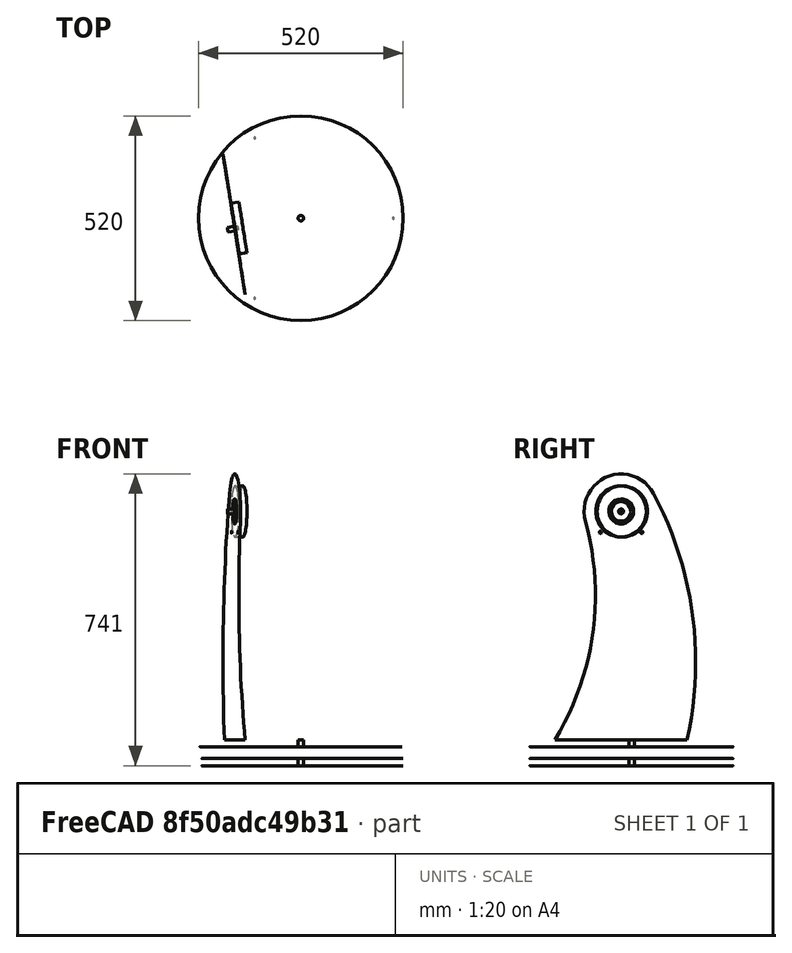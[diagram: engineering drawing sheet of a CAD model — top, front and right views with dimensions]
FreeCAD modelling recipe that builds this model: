
FCSTD DOCUMENT  (FreeCAD 2020.12.13R23076 +3015 (Git))
Label: teleskop
License: All rights reserved
LicenseURL: http://en.wikipedia.org/wiki/All_rights_reserved
objects: Part::FeaturePython×19, App::FeaturePython×13, App::Link×3
note: 18 computed .brp shape members not serialized (recipe doc carries the construction recipe); baked Part::Feature solids carry a one-line shape summary decoded from their .brp
EXTERNAL_REF file=zawieszenie-dol.fcstd obj=Assembly
EXTERNAL_REF file=zawieszenia-gora.fcstd obj=Assembly
EXTERNAL_REF file=tubus-kpl.FCStd obj=Assembly

FEATURE [App::Link] Link  label="zawieszenie-dol"
  LinkPlacement = pos=(-3.50003,-2.00002,205) rot=(0,0,1;0rad)
  LinkedObject = -> <external zawieszenie-dol.fcstd>#Assembly
  Placement = pos=(-3.50003,-2.00002,205) rot=(0,0,1;0rad)
  SyncGroupVisibility = false
  _LinkVersion = 1
FEATURE [App::Link] Link001  label="zawieszenie-gora"
  LinkPlacement = pos=(105.826,17.307,58.0003) rot=(0,0,1;0.156782rad)
  LinkedObject = -> <external zawieszenia-gora.fcstd>#Assembly
  Placement = pos=(105.826,17.307,58.0003) rot=(0,0,1;0.156782rad)
  SyncGroupVisibility = false
  _LinkVersion = 1
FEATURE [App::Link] Link002  label="tubus-kpl"
  LinkPlacement = pos=(89.4728,-455.647,570.496) rot=(-0.038514,0.490302,0.870701;3.27817rad)
  LinkedObject = -> <external tubus-kpl.FCStd>#Assembly
  Placement = pos=(89.4728,-455.647,570.496) rot=(-0.038514,0.490302,0.870701;3.27817rad)
  SyncGroupVisibility = false
  _LinkVersion = 1
FEATURE [Part::FeaturePython] Parts  # WARN: FeaturePython — macro-defined, semantics opaque (R4)
  Group = -> [Link,Link001,Link002]
  GroupMode = 0
  _LinkVersion = 1
FEATURE [Part::FeaturePython] Assembly  label="teleskop"  # WARN: FeaturePython — macro-defined, semantics opaque (R4)
  AutoRelax = true
  BuildShape = 0
  Freeze = false
  Group = -> [Constraints,Elements,Parts]
  Verbose = false
  _LinkVersion = 1
  _SolverType = 1
  _Version = 1
FEATURE [App::FeaturePython] Constraints  # WARN: FeaturePython — macro-defined, semantics opaque (R4)
  Group = -> [Constraint,Constraint001,Constraint002,Constraint003]
  _LinkVersion = 1
  _Version = 1
FEATURE [App::FeaturePython] Elements  # WARN: FeaturePython — macro-defined, semantics opaque (R4)
  Group = -> [_Element,_Element001,_Element002,_Element003,_Element004,_Element005,_Element006,_Element008,_Element010,_Element011,_Element012,_Element013,_Element016,_Element017,_Element018,_Element019,_Element020]
  _LinkVersion = 1
FEATURE [Part::FeaturePython] _Element  # link proxy (typed FeaturePython)
  Detach = false
  LinkTransform = true
  LinkedObject = -> Link001 [1.$Element025.]
  _LinkVersion = 1
  _Parent = -> Elements
FEATURE [Part::FeaturePython] _Element001  # link proxy (typed FeaturePython)
  Detach = false
  LinkTransform = true
  LinkedObject = -> Link [1.$Element.]
  _LinkVersion = 1
  _Parent = -> Elements
FEATURE [Part::FeaturePython] _Element002  # link proxy (typed FeaturePython)
  Detach = false
  LinkTransform = true
  LinkedObject = -> Link [1.$Element001.]
  _LinkVersion = 1
  _Parent = -> Elements
FEATURE [Part::FeaturePython] _Element003  # link proxy (typed FeaturePython)
  Detach = false
  LinkTransform = true
  LinkedObject = -> Link001 [1.$Element026.]
  _LinkVersion = 1
  _Parent = -> Elements
FEATURE [Part::FeaturePython] _Element004  # link proxy (typed FeaturePython)
  Detach = false
  LinkTransform = true
  LinkedObject = -> Link001 [1.$Element027.]
  _LinkVersion = 1
  _Parent = -> Elements
FEATURE [Part::FeaturePython] _Element005  # link proxy (typed FeaturePython)
  Detach = false
  LinkTransform = true
  LinkedObject = -> Link [1.$_Element017.]
  _LinkVersion = 1
  _Parent = -> Elements
FEATURE [Part::FeaturePython] _Element006  # link proxy (typed FeaturePython)
  Detach = false
  LinkTransform = true
  LinkedObject = -> Link002 [1.$Element.]
  _LinkVersion = 1
  _Parent = -> Elements
FEATURE [Part::FeaturePython] _Element008  # link proxy (typed FeaturePython)
  Detach = false
  LinkTransform = true
  LinkedObject = -> Link002 [1.$Element001.]
  _LinkVersion = 1
  _Parent = -> Elements
FEATURE [Part::FeaturePython] _Element010  # link proxy (typed FeaturePython)
  Detach = false
  LinkTransform = true
  LinkedObject = -> Link002 [1.$Element002.]
  _LinkVersion = 1
  _Parent = -> Elements
FEATURE [Part::FeaturePython] _Element011  # link proxy (typed FeaturePython)
  Detach = false
  LinkTransform = true
  LinkedObject = -> Link002 [1.$Element003.]
  _LinkVersion = 1
  _Parent = -> Elements
FEATURE [Part::FeaturePython] _Element012  # link proxy (typed FeaturePython)
  Detach = false
  LinkTransform = true
  LinkedObject = -> Link001 [1.$Element028.]
  _LinkVersion = 1
  _Parent = -> Elements
FEATURE [Part::FeaturePython] _Element013  # link proxy (typed FeaturePython)
  Detach = false
  LinkTransform = true
  LinkedObject = -> Link002 [1.$Element004.]
  _LinkVersion = 1
  _Parent = -> Elements
FEATURE [Part::FeaturePython] _Element016  # link proxy (typed FeaturePython)
  Detach = false
  LinkTransform = true
  LinkedObject = -> Link002 [1.$Element005.]
  _LinkVersion = 1
  _Parent = -> Elements
FEATURE [Part::FeaturePython] _Element017  # link proxy (typed FeaturePython)
  Detach = false
  LinkTransform = true
  LinkedObject = -> Link001 [1.$Element029.]
  _LinkVersion = 1
  _Parent = -> Elements
FEATURE [Part::FeaturePython] _Element018  # link proxy (typed FeaturePython)
  Detach = false
  LinkTransform = true
  LinkedObject = -> Link001 [1.$Element030.]
  _LinkVersion = 1
  _Parent = -> Elements
FEATURE [Part::FeaturePython] _Element019  # link proxy (typed FeaturePython)
  Detach = false
  LinkTransform = true
  LinkedObject = -> Link001 [1.$Element031.]
  _LinkVersion = 1
  _Parent = -> Elements
FEATURE [Part::FeaturePython] _Element020  # link proxy (typed FeaturePython)
  Detach = false
  LinkTransform = true
  LinkedObject = -> Link [1.$_Element018.]
  _LinkVersion = 1
  _Parent = -> Elements
FEATURE [App::FeaturePython] Constraint  label="Locked"  # WARN: FeaturePython — macro-defined, semantics opaque (R4)
  Disabled = false
  Group = -> [ElementLink]
  _ConstraintType = 0
  _LinkVersion = 1
  _Parent = -> Constraints
FEATURE [App::FeaturePython] ElementLink  label="_Element020"  # link proxy (typed FeaturePython)
  LinkTransform = true
  LinkedObject = -> _Element020
  _LinkVersion = 1
  _Parent = -> Constraint
FEATURE [App::FeaturePython] Constraint001  label="PlaneCoincident"  # WARN: FeaturePython — macro-defined, semantics opaque (R4)
  Angle = 0
  AnglePitch = 0
  AngleRoll = 0
  Cascade = false
  Disabled = false
  Group = -> [ElementLink001,ElementLink002]
  LockAngle = false
  Multiply = false
  Offset = -30
  OffsetX = 0
  OffsetY = 0
  _ConstraintType = 35
  _LinkVersion = 1
  _Parent = -> Constraints
FEATURE [App::FeaturePython] ElementLink001  label="_Element005"  # link proxy (typed FeaturePython)
  LinkTransform = true
  LinkedObject = -> _Element005
  _LinkVersion = 1
  _Parent = -> Constraint001
FEATURE [App::FeaturePython] ElementLink002  label="_Element004"  # link proxy (typed FeaturePython)
  LinkTransform = true
  LinkedObject = -> _Element004
  _LinkVersion = 1
  _Parent = -> Constraint001
FEATURE [App::FeaturePython] Constraint002  label="AxialAlignment"  # WARN: FeaturePython — macro-defined, semantics opaque (R4)
  Angle = 0
  AnglePitch = 0
  AngleRoll = 0
  Disabled = false
  Group = -> [ElementLink003,ElementLink004]
  LockAngle = false
  Multiply = false
  _ConstraintType = 36
  _LinkVersion = 1
  _Parent = -> Constraints
FEATURE [App::FeaturePython] ElementLink003  label="_Element006"  # link proxy (typed FeaturePython)
  LinkTransform = true
  LinkedObject = -> _Element006
  _LinkVersion = 1
  _Parent = -> Constraint002
FEATURE [App::FeaturePython] ElementLink004  label="_Element017"  # link proxy (typed FeaturePython)
  LinkTransform = true
  LinkedObject = -> _Element017
  _LinkVersion = 1
  _Parent = -> Constraint002
FEATURE [App::FeaturePython] Constraint003  label="PointInPlane"  # WARN: FeaturePython — macro-defined, semantics opaque (R4)
  Disabled = false
  Group = -> [ElementLink005,ElementLink006]
  _ConstraintType = 3
  _LinkVersion = 1
  _Parent = -> Constraints
FEATURE [App::FeaturePython] ElementLink005  label="_Element019"  # link proxy (typed FeaturePython)
  LinkTransform = true
  LinkedObject = -> _Element019
  _LinkVersion = 1
  _Parent = -> Constraint003
FEATURE [App::FeaturePython] ElementLink006  label="_Element010"  # link proxy (typed FeaturePython)
  LinkTransform = true
  LinkedObject = -> _Element010
  _LinkVersion = 1
  _Parent = -> Constraint003

RESOLVED EXTERNAL PARTS (link-assembly join: the EXTERNAL_REF files above that resolve inside this repo's crawl, each included once):
---- part tubus-kpl.FCStd = doc fcstd_3efcf8065df4 ----
FCSTD DOCUMENT  (FreeCAD 2020.12.13R23076 +3015 (Git))
Label: tubus-kpl
License: All rights reserved
LicenseURL: http://en.wikipedia.org/wiki/All_rights_reserved
objects: Part::FeaturePython×12, App::FeaturePython×8, App::Link×2
note: 11 computed .brp shape members not serialized (recipe doc carries the construction recipe); baked Part::Feature solids carry a one-line shape summary decoded from their .brp
EXTERNAL_REF file=tubus.fcstd obj=Body
EXTERNAL_REF file=wieniec-rury-mod1high.FCStd obj=Body

FEATURE [App::Link] Link  label="tubus"
  LinkPlacement = pos=(19.9999,-8.40128e-05,121) rot=(0,0.707107,0.707107;0rad)
  LinkedObject = -> <external tubus.fcstd>#Body
  Placement = pos=(19.9999,-8.40128e-05,121) rot=(0,0.707107,0.707107;0rad)
  SyncGroupVisibility = false
  _LinkVersion = 1
FEATURE [App::Link] Link001  label="wieniec-rury"
  LinkPlacement = pos=(155,-6.79195e-05,541) rot=(0.57735,0.57735,0.57735;2.0944rad)
  LinkedObject = -> <external wieniec-rury-mod1high.FCStd>#Body
  Placement = pos=(155,-6.79195e-05,541) rot=(0.57735,0.57735,0.57735;2.0944rad)
  SyncGroupVisibility = false
  _LinkVersion = 1
FEATURE [Part::FeaturePython] Parts  # WARN: FeaturePython — macro-defined, semantics opaque (R4)
  Group = -> [Link,Link001]
  GroupMode = 0
  _LinkVersion = 1
FEATURE [Part::FeaturePython] Assembly  label="tubus-kpl"  # WARN: FeaturePython — macro-defined, semantics opaque (R4)
  AutoRelax = true
  BuildShape = 0
  Freeze = true
  Group = -> [Constraints,Elements,Parts]
  Verbose = false
  _LinkVersion = 1
  _SolverType = 1
  _Version = 1
FEATURE [App::FeaturePython] Constraints  # WARN: FeaturePython — macro-defined, semantics opaque (R4)
  Group = -> [Constraint,Constraint001]
  _LinkVersion = 1
  _Version = 1
FEATURE [App::FeaturePython] Elements  # WARN: FeaturePython — macro-defined, semantics opaque (R4)
  Group = -> [_Element,_Element001,_Element002,_Element003,Element,Element001,Element002,Element003,Element004,Element005]
  _LinkVersion = 1
FEATURE [App::FeaturePython] Constraint  label="AxialAlignment"  # WARN: FeaturePython — macro-defined, semantics opaque (R4)
  Angle = 0
  AnglePitch = 0
  AngleRoll = 0
  Disabled = false
  Group = -> [ElementLink,ElementLink001]
  LockAngle = false
  Multiply = false
  _ConstraintType = 36
  _LinkVersion = 1
  _Parent = -> Constraints
FEATURE [App::FeaturePython] ElementLink  label="_Element"  # link proxy (typed FeaturePython)
  LinkTransform = true
  LinkedObject = -> _Element
  _LinkVersion = 1
  _Parent = -> Constraint
FEATURE [Part::FeaturePython] _Element  # link proxy (typed FeaturePython)
  Detach = false
  LinkTransform = true
  LinkedObject = -> Link001 [Pocket007.Face15]
  _LinkVersion = 1
  _Parent = -> Elements
FEATURE [App::FeaturePython] ElementLink001  label="_Element001"  # link proxy (typed FeaturePython)
  LinkTransform = true
  LinkedObject = -> _Element001
  _LinkVersion = 1
  _Parent = -> Constraint
FEATURE [Part::FeaturePython] _Element001  # link proxy (typed FeaturePython)
  Detach = false
  LinkTransform = true
  LinkedObject = -> Link [Pocket003.Face2]
  _LinkVersion = 1
  _Parent = -> Elements
FEATURE [App::FeaturePython] Constraint001  label="AxialAlignment001"  # WARN: FeaturePython — macro-defined, semantics opaque (R4)
  Angle = 0
  AnglePitch = 0
  AngleRoll = 0
  Disabled = false
  Group = -> [ElementLink002,ElementLink003]
  LockAngle = false
  Multiply = false
  _ConstraintType = 36
  _LinkVersion = 1
  _Parent = -> Constraints
FEATURE [App::FeaturePython] ElementLink002  label="_Element002"  # link proxy (typed FeaturePython)
  LinkTransform = true
  LinkedObject = -> _Element002
  _LinkVersion = 1
  _Parent = -> Constraint001
FEATURE [Part::FeaturePython] _Element002  # link proxy (typed FeaturePython)
  Detach = false
  LinkTransform = true
  LinkedObject = -> Link001 [Pocket007.Face6]
  _LinkVersion = 1
  _Parent = -> Elements
FEATURE [App::FeaturePython] ElementLink003  label="_Element003"  # link proxy (typed FeaturePython)
  LinkTransform = true
  LinkedObject = -> _Element003
  _LinkVersion = 1
  _Parent = -> Constraint001
FEATURE [Part::FeaturePython] _Element003  # link proxy (typed FeaturePython)
  Detach = false
  LinkTransform = true
  LinkedObject = -> Link [Pocket003.Face1]
  _LinkVersion = 1
  _Parent = -> Elements
FEATURE [Part::FeaturePython] Element  # link proxy (typed FeaturePython)
  Detach = false
  LinkTransform = true
  LinkedObject = -> Link [Pocket003.Face25]
  _LinkVersion = 1
  _Parent = -> Elements
FEATURE [Part::FeaturePython] Element001  # link proxy (typed FeaturePython)
  Detach = false
  LinkTransform = true
  LinkedObject = -> Link [Pocket003.Face14]
  _LinkVersion = 1
  _Parent = -> Elements
FEATURE [Part::FeaturePython] Element002  # link proxy (typed FeaturePython)
  Detach = false
  LinkTransform = true
  LinkedObject = -> Link [Pocket003.Face19]
  _LinkVersion = 1
  _Parent = -> Elements
FEATURE [Part::FeaturePython] Element003  # link proxy (typed FeaturePython)
  Detach = false
  LinkTransform = true
  LinkedObject = -> Link [Pocket003.Edge40]
  _LinkVersion = 1
  _Parent = -> Elements
FEATURE [Part::FeaturePython] Element004  # link proxy (typed FeaturePython)
  Detach = false
  LinkTransform = true
  LinkedObject = -> Link [Pocket003.Edge34]
  _LinkVersion = 1
  _Parent = -> Elements
FEATURE [Part::FeaturePython] Element005  # link proxy (typed FeaturePython)
  Detach = false
  LinkTransform = true
  LinkedObject = -> Link [Pocket003.Face10]
  _LinkVersion = 1
  _Parent = -> Elements
---- part zawieszenia-gora.fcstd = doc fcstd_c8abc18c9d7d (55000 chars; too large to inline — full recipe in that document) ----
---- part zawieszenie-dol.fcstd = doc fcstd_90b82e9d4289 ----
FCSTD DOCUMENT  (FreeCAD 2020.12.13R23076 +3015 (Git))
Label: zawieszenie-dol
License: All rights reserved
LicenseURL: http://en.wikipedia.org/wiki/All_rights_reserved
objects: App::FeaturePython×64, Part::FeaturePython×34, App::Link×12, App::LinkElement×6
note: 33 computed .brp shape members not serialized (recipe doc carries the construction recipe); baked Part::Feature solids carry a one-line shape summary decoded from their .brp
EXTERNAL_REF file=plyta-okr-dol.fcstd obj=Body
EXTERNAL_REF file=stopa.fcstd obj=Body
EXTERNAL_REF file=wieniec_mod1.FCStd obj=Body
EXTERNAL_REF file=tulejka-sruby.FCStd obj=Body
EXTERNAL_REF file=piasta-lozyska.FCStd obj=Body
EXTERNAL_REF file=lozysko 51126.FCStd obj=Assembly
EXTERNAL_REF file=regulacja-nogi.FCStd obj=Assembly

FEATURE [App::Link] Link  label="Link_plyta-okr-dol"
  LinkedObject = -> <external plyta-okr-dol.fcstd>#Body
  SyncGroupVisibility = false
  _LinkVersion = 1
FEATURE [App::Link] Link001  label="Link001_Assembly"
  LinkedObject = -> Assembly
  SyncGroupVisibility = false
  _LinkVersion = 1
FEATURE [App::Link] Link002  label="Link002_stopa"
  LinkPlacement = pos=(235,0,0) rot=(0,0,1;0rad)
  LinkedObject = -> <external stopa.fcstd>#Body
  Placement = pos=(235,0,0) rot=(0,0,1;0rad)
  SyncGroupVisibility = false
  _LinkVersion = 1
FEATURE [App::Link] Link003  label="Link003_Assembly"
  LinkedObject = -> Assembly
  SyncGroupVisibility = false
  _LinkVersion = 1
FEATURE [App::Link] Link004  label="Link004_Assembly"
  LinkedObject = -> Assembly
  SyncGroupVisibility = false
  _LinkVersion = 1
FEATURE [App::Link] Link005  label="Link005_stopa"
  LinkPlacement = pos=(-117.5,203.516,0) rot=(0,0,1;0rad)
  LinkedObject = -> <external stopa.fcstd>#Body
  Placement = pos=(-117.5,203.516,0) rot=(0,0,1;0rad)
  SyncGroupVisibility = false
  _LinkVersion = 1
FEATURE [App::Link] Link006  label="Link006_stopa"
  LinkPlacement = pos=(-117.5,-203.516,0) rot=(0,0,1;0rad)
  LinkedObject = -> <external stopa.fcstd>#Body
  Placement = pos=(-117.5,-203.516,0) rot=(0,0,1;0rad)
  SyncGroupVisibility = false
  _LinkVersion = 1
FEATURE [App::Link] Link008  label="tulejka-sruby"
  LinkPlacement = pos=(0,0,-4.40707e-10) rot=(0,0,1;0rad)
  LinkedObject = -> <external tulejka-sruby.FCStd>#Body
  Placement = pos=(0,0,-4.40707e-10) rot=(0,0,1;0rad)
  SyncGroupVisibility = false
  _LinkVersion = 1
FEATURE [App::Link] Link009  label="piasta-lozyska"
  LinkPlacement = pos=(0,0,18) rot=(0,0,1;0rad)
  LinkedObject = -> <external piasta-lozyska.FCStd>#Body
  Placement = pos=(0,0,18) rot=(0,0,1;0rad)
  SyncGroupVisibility = false
  _LinkVersion = 1
FEATURE [App::Link] Link010  label="51126-lozysko"
  LinkPlacement = pos=(0,0,18) rot=(0,-1,0;1.5708rad)
  LinkedObject = -> <external lozysko 51126.FCStd>#Assembly
  Placement = pos=(0,0,18) rot=(0,-1,0;1.5708rad)
  SyncGroupVisibility = false
  _LinkVersion = 1
FEATURE [App::LinkElement] Link011_i0
  LinkPlacement = pos=(0,0,1.8261e-12) rot=(0,0,1;0rad)
  LinkedObject = -> <external regulacja-nogi.FCStd>#Assembly
  Placement = pos=(0,0,1.8261e-12) rot=(0,0,1;0rad)
  _LinkVersion = 1
FEATURE [App::LinkElement] Link011_i1
  LinkPlacement = pos=(-203.516,-352.5,1.8296e-12) rot=(0,0,-1;1.0472rad)
  LinkedObject = -> <external regulacja-nogi.FCStd>#Assembly
  Placement = pos=(-203.516,-352.5,1.8296e-12) rot=(0,0,-1;1.0472rad)
  _LinkVersion = 1
FEATURE [App::LinkElement] Link011_i2
  LinkPlacement = pos=(203.516,-352.5,1.8296e-12) rot=(0,0,1;1.0472rad)
  LinkedObject = -> <external regulacja-nogi.FCStd>#Assembly
  Placement = pos=(203.516,-352.5,1.8296e-12) rot=(0,0,1;1.0472rad)
  _LinkVersion = 1
FEATURE [App::Link] Link011  label="regulacja-nogi"
  ElementCount = 3
  ElementList = -> [Link011_i0,Link011_i1,Link011_i2]
  LinkPlacement = pos=(235,0,-20) rot=(0.707107,0.707107,0;3.14159rad)
  LinkedObject = -> <external regulacja-nogi.FCStd>#Assembly
  Placement = pos=(235,0,-20) rot=(0.707107,0.707107,0;3.14159rad)
  SyncGroupVisibility = false
  _LinkVersion = 1
FEATURE [App::LinkElement] Link007_i0
  LinkPlacement = pos=(0,0,-3.6e-15) rot=(0,0,-1;5.65256rad)
  LinkedObject = -> <external wieniec_mod1.FCStd>#Body
  Placement = pos=(0,0,-3.6e-15) rot=(0,0,-1;5.65256rad)
  _LinkVersion = 0
FEATURE [App::LinkElement] Link007_i1
  LinkPlacement = pos=(2e-16,8e-16,3.6e-15) rot=(0,0,-1;4.77196rad)
  LinkedObject = -> <external wieniec_mod1.FCStd>#Body
  Placement = pos=(2e-16,8e-16,3.6e-15) rot=(0,0,-1;4.77196rad)
  _LinkVersion = 0
FEATURE [App::LinkElement] Link007_i2
  LinkPlacement = pos=(-1.93e-14,2.3e-15,2.49e-14) rot=(0,0,-1;0.249973rad)
  LinkedObject = -> <external wieniec_mod1.FCStd>#Body
  Placement = pos=(-1.93e-14,2.3e-15,2.49e-14) rot=(0,0,-1;0.249973rad)
  _LinkVersion = 0
FEATURE [App::Link] Link007  label="wieniec"
  ElementCount = 3
  ElementList = -> [Link007_i0,Link007_i1,Link007_i2]
  LinkPlacement = pos=(0,0,22) rot=(0.991445,-0.130526,0;3.14159rad)
  LinkedObject = -> <external wieniec_mod1.FCStd>#Body
  Placement = pos=(0,0,22) rot=(0.991445,-0.130526,0;3.14159rad)
  SyncGroupVisibility = false
  _LinkVersion = 1
FEATURE [Part::FeaturePython] Parts  # WARN: FeaturePython — macro-defined, semantics opaque (R4)
  Group = -> [Link,Link002,Link005,Link006,Link007,Link008,Link009,Link010,Link011]
  GroupMode = 0
  _LinkVersion = 1
FEATURE [Part::FeaturePython] Assembly  label="zawieszenie-dol"  # WARN: FeaturePython — macro-defined, semantics opaque (R4)
  AutoRelax = true
  BuildShape = 0
  Freeze = true
  Group = -> [Constraints,Elements,Parts]
  Verbose = false
  _LinkVersion = 1
  _SolverType = 1
FEATURE [App::FeaturePython] Constraints  # WARN: FeaturePython — macro-defined, semantics opaque (R4)
  Group = -> [Constraint001,Constraint002,Constraint003,Constraint004,Constraint005,Constraint006,Constraint,Constraint011,Constraint012,Constraint013,Constraint014,Constraint015,Constraint016,Constraint017,Constraint018,Constraint019,Constraint020,Constraint021,Constraint022,Constraint023,Constraint024]
  _LinkVersion = 1
  _Version = 1
FEATURE [App::FeaturePython] Elements  # WARN: FeaturePython — macro-defined, semantics opaque (R4)
  Group = -> [_Element,_Element001,_Element002,_Element003,_Element004,_Element005,_Element006,_Element007,_Element008,_Element009,_Element011,_Element013,_Element015,_Element017,Element,Element001,_Element018,_Element019,_Element020,_Element021,_Element022,_Element023,_Element024,_Element025,_Element026,_Element027,_Element028,_Element029,_Element030,_Element031,_Element032,_Element033]
  _LinkVersion = 1
FEATURE [Part::FeaturePython] _Element  # link proxy (typed FeaturePython)
  Detach = false
  LinkTransform = true
  LinkedObject = -> Link [PolarPattern.Face2]
  _LinkVersion = 1
  _Parent = -> Elements
FEATURE [App::FeaturePython] Constraint001  label="AxialAlignment"  # WARN: FeaturePython — macro-defined, semantics opaque (R4)
  Angle = 0
  AnglePitch = 0
  AngleRoll = 0
  Disabled = false
  Group = -> [ElementLink001,ElementLink002]
  LockAngle = false
  Multiply = false
  _ConstraintType = 36
  _LinkVersion = 1
  _Parent = -> Constraints
FEATURE [App::FeaturePython] ElementLink001  label="_Element001"  # link proxy (typed FeaturePython)
  LinkTransform = true
  LinkedObject = -> _Element001
  _LinkVersion = 1
  _Parent = -> Constraint001
FEATURE [Part::FeaturePython] _Element001  # link proxy (typed FeaturePython)
  Detach = false
  LinkTransform = true
  LinkedObject = -> Link005 [Revolution.Edge1]
  _LinkVersion = 1
  _Parent = -> Elements
FEATURE [App::FeaturePython] ElementLink002  label="_Element002"  # link proxy (typed FeaturePython)
  LinkTransform = true
  LinkedObject = -> _Element002
  _LinkVersion = 1
  _Parent = -> Constraint001
FEATURE [Part::FeaturePython] _Element002  # link proxy (typed FeaturePython)
  Detach = false
  LinkTransform = true
  LinkedObject = -> Link [PolarPattern.Edge6]
  _LinkVersion = 1
  _Parent = -> Elements
FEATURE [App::FeaturePython] Constraint002  label="PlaneAlignment"  # WARN: FeaturePython — macro-defined, semantics opaque (R4)
  Angle = 0
  AnglePitch = 0
  AngleRoll = 0
  Cascade = false
  Disabled = false
  Group = -> [ElementLink003,ElementLink004]
  LockAngle = false
  _ConstraintType = 37
  _LinkVersion = 1
  _Parent = -> Constraints
FEATURE [App::FeaturePython] ElementLink003  label="_Element"  # link proxy (typed FeaturePython)
  LinkTransform = true
  LinkedObject = -> _Element
  _LinkVersion = 1
  _Parent = -> Constraint002
FEATURE [App::FeaturePython] ElementLink004  label="_Element003"  # link proxy (typed FeaturePython)
  LinkTransform = true
  LinkedObject = -> _Element003
  _LinkVersion = 1
  _Parent = -> Constraint002
FEATURE [Part::FeaturePython] _Element003  # link proxy (typed FeaturePython)
  Detach = false
  LinkTransform = true
  LinkedObject = -> Link005 [Revolution.Face1]
  _LinkVersion = 1
  _Parent = -> Elements
FEATURE [App::FeaturePython] Constraint003  label="AxialAlignment001"  # WARN: FeaturePython — macro-defined, semantics opaque (R4)
  Angle = 0
  AnglePitch = 0
  AngleRoll = 0
  Disabled = false
  Group = -> [ElementLink005,ElementLink006]
  LockAngle = false
  Multiply = false
  _ConstraintType = 36
  _LinkVersion = 1
  _Parent = -> Constraints
FEATURE [App::FeaturePython] ElementLink005  label="_Element004"  # link proxy (typed FeaturePython)
  LinkTransform = true
  LinkedObject = -> _Element004
  _LinkVersion = 1
  _Parent = -> Constraint003
FEATURE [Part::FeaturePython] _Element004  # link proxy (typed FeaturePython)
  Detach = false
  LinkTransform = true
  LinkedObject = -> Link006 [Revolution.Edge1]
  _LinkVersion = 1
  _Parent = -> Elements
FEATURE [App::FeaturePython] ElementLink006  label="_Element005"  # link proxy (typed FeaturePython)
  LinkTransform = true
  LinkedObject = -> _Element005
  _LinkVersion = 1
  _Parent = -> Constraint003
FEATURE [Part::FeaturePython] _Element005  # link proxy (typed FeaturePython)
  Detach = false
  LinkTransform = true
  LinkedObject = -> Link [PolarPattern.Edge4]
  _LinkVersion = 1
  _Parent = -> Elements
FEATURE [App::FeaturePython] Constraint004  label="PlaneAlignment001"  # WARN: FeaturePython — macro-defined, semantics opaque (R4)
  Angle = 0
  AnglePitch = 0
  AngleRoll = 0
  Cascade = false
  Disabled = false
  Group = -> [ElementLink007,ElementLink008]
  LockAngle = false
  _ConstraintType = 37
  _LinkVersion = 1
  _Parent = -> Constraints
FEATURE [App::FeaturePython] ElementLink007  label="_Element"  # link proxy (typed FeaturePython)
  LinkTransform = true
  LinkedObject = -> _Element
  _LinkVersion = 1
  _Parent = -> Constraint004
FEATURE [App::FeaturePython] ElementLink008  label="_Element006"  # link proxy (typed FeaturePython)
  LinkTransform = true
  LinkedObject = -> _Element006
  _LinkVersion = 1
  _Parent = -> Constraint004
FEATURE [Part::FeaturePython] _Element006  # link proxy (typed FeaturePython)
  Detach = false
  LinkTransform = true
  LinkedObject = -> Link006 [Revolution.Face1]
  _LinkVersion = 1
  _Parent = -> Elements
FEATURE [App::FeaturePython] Constraint005  label="AxialAlignment002"  # WARN: FeaturePython — macro-defined, semantics opaque (R4)
  Angle = 0
  AnglePitch = 0
  AngleRoll = 0
  Disabled = false
  Group = -> [ElementLink009,ElementLink010]
  LockAngle = false
  Multiply = false
  _ConstraintType = 36
  _LinkVersion = 1
  _Parent = -> Constraints
FEATURE [App::FeaturePython] ElementLink009  label="_Element007"  # link proxy (typed FeaturePython)
  LinkTransform = true
  LinkedObject = -> _Element007
  _LinkVersion = 1
  _Parent = -> Constraint005
FEATURE [Part::FeaturePython] _Element007  # link proxy (typed FeaturePython)
  Detach = false
  LinkTransform = true
  LinkedObject = -> Link002 [Revolution.Edge1]
  _LinkVersion = 1
  _Parent = -> Elements
FEATURE [App::FeaturePython] ElementLink010  label="_Element008"  # link proxy (typed FeaturePython)
  LinkTransform = true
  LinkedObject = -> _Element008
  _LinkVersion = 1
  _Parent = -> Constraint005
FEATURE [Part::FeaturePython] _Element008  # link proxy (typed FeaturePython)
  Detach = false
  LinkTransform = true
  LinkedObject = -> Link [PolarPattern.Edge5]
  _LinkVersion = 1
  _Parent = -> Elements
FEATURE [App::FeaturePython] Constraint006  label="PlaneAlignment002"  # WARN: FeaturePython — macro-defined, semantics opaque (R4)
  Angle = 0
  AnglePitch = 0
  AngleRoll = 0
  Cascade = false
  Disabled = false
  Group = -> [ElementLink011,ElementLink012]
  LockAngle = false
  _ConstraintType = 37
  _LinkVersion = 1
  _Parent = -> Constraints
FEATURE [App::FeaturePython] ElementLink011  label="_Element"  # link proxy (typed FeaturePython)
  LinkTransform = true
  LinkedObject = -> _Element
  _LinkVersion = 1
  _Parent = -> Constraint006
FEATURE [App::FeaturePython] ElementLink012  label="_Element009"  # link proxy (typed FeaturePython)
  LinkTransform = true
  LinkedObject = -> _Element009
  _LinkVersion = 1
  _Parent = -> Constraint006
FEATURE [Part::FeaturePython] _Element009  # link proxy (typed FeaturePython)
  Detach = false
  LinkTransform = true
  LinkedObject = -> Link002 [Revolution.Face1]
  _LinkVersion = 1
  _Parent = -> Elements
FEATURE [Part::FeaturePython] _Element011  # link proxy (typed FeaturePython)
  Detach = false
  LinkTransform = true
  LinkedObject = -> Link [PolarPattern.Face1]
  _LinkVersion = 1
  _Parent = -> Elements
FEATURE [Part::FeaturePython] _Element013  # link proxy (typed FeaturePython)
  Detach = false
  LinkTransform = true
  LinkedObject = -> Link [PolarPattern.Face3]
  _LinkVersion = 1
  _Parent = -> Elements
FEATURE [Part::FeaturePython] _Element015  # link proxy (typed FeaturePython)
  Detach = false
  LinkTransform = true
  LinkedObject = -> Link [Pocket001.Face1]
  _LinkVersion = 1
  _Parent = -> Elements
FEATURE [Part::FeaturePython] _Element017  # link proxy (typed FeaturePython)
  Detach = false
  LinkTransform = true
  LinkedObject = -> Link [Pocket001.Face3]
  _LinkVersion = 1
  _Parent = -> Elements
FEATURE [Part::FeaturePython] Element  # link proxy (typed FeaturePython)
  Detach = false
  LinkTransform = true
  LinkedObject = -> Link [Pocket001.Face5]
  _LinkVersion = 1
  _Parent = -> Elements
FEATURE [Part::FeaturePython] Element001  # link proxy (typed FeaturePython)
  Detach = false
  LinkTransform = true
  LinkedObject = -> Link [Pocket001.Edge5]
  _LinkVersion = 1
  _Parent = -> Elements
FEATURE [App::FeaturePython] Constraint  label="Locked"  # WARN: FeaturePython — macro-defined, semantics opaque (R4)
  Disabled = false
  Group = -> [ElementLink]
  _ConstraintType = 0
  _LinkVersion = 1
  _Parent = -> Constraints
FEATURE [App::FeaturePython] ElementLink  label="_Element018"  # link proxy (typed FeaturePython)
  LinkTransform = true
  LinkedObject = -> _Element018
  _LinkVersion = 1
  _Parent = -> Constraint
FEATURE [Part::FeaturePython] _Element018  # link proxy (typed FeaturePython)
  Detach = false
  LinkTransform = true
  LinkedObject = -> Link [Pocket001.Face2]
  _LinkVersion = 1
  _Parent = -> Elements
FEATURE [Part::FeaturePython] _Element019  # link proxy (typed FeaturePython)
  Detach = false
  LinkTransform = true
  LinkedObject = -> Link008 [Chamfer.Face1]
  _LinkVersion = 1
  _Parent = -> Elements
FEATURE [Part::FeaturePython] _Element020  # link proxy (typed FeaturePython)
  Detach = false
  LinkTransform = true
  LinkedObject = -> Link008 [Chamfer.Face3]
  _LinkVersion = 1
  _Parent = -> Elements
FEATURE [App::FeaturePython] Constraint011  label="PlaneCoincident"  # WARN: FeaturePython — macro-defined, semantics opaque (R4)
  Angle = 0
  AnglePitch = 0
  AngleRoll = 0
  Cascade = false
  Disabled = false
  Group = -> [ElementLink021,ElementLink022]
  LockAngle = false
  Multiply = false
  OffsetX = 0
  OffsetY = 0
  _ConstraintType = 35
  _LinkVersion = 1
  _Parent = -> Constraints
FEATURE [App::FeaturePython] ElementLink021  label="_Element021"  # link proxy (typed FeaturePython)
  LinkTransform = true
  LinkedObject = -> _Element021
  _LinkVersion = 1
  _Parent = -> Constraint011
FEATURE [Part::FeaturePython] _Element021  # link proxy (typed FeaturePython)
  Detach = false
  LinkTransform = true
  LinkedObject = -> Link009 [Pocket002.Face1]
  _LinkVersion = 1
  _Parent = -> Elements
FEATURE [App::FeaturePython] ElementLink022  label="_Element017"  # link proxy (typed FeaturePython)
  LinkTransform = true
  LinkedObject = -> _Element017
  _LinkVersion = 1
  _Parent = -> Constraint011
FEATURE [App::FeaturePython] Constraint012  label="PlaneCoincident001"  # WARN: FeaturePython — macro-defined, semantics opaque (R4)
  Angle = 0
  AnglePitch = 0
  AngleRoll = 0
  Cascade = false
  Disabled = false
  Group = -> [ElementLink023,ElementLink024]
  LockAngle = false
  Multiply = false
  OffsetX = 0
  OffsetY = 0
  _ConstraintType = 35
  _LinkVersion = 1
  _Parent = -> Constraints
FEATURE [App::FeaturePython] ElementLink023  label="_Element020"  # link proxy (typed FeaturePython)
  LinkTransform = true
  LinkedObject = -> _Element020
  _LinkVersion = 1
  _Parent = -> Constraint012
FEATURE [App::FeaturePython] ElementLink024  label="_Element018"  # link proxy (typed FeaturePython)
  LinkTransform = true
  LinkedObject = -> _Element018
  _LinkVersion = 1
  _Parent = -> Constraint012
FEATURE [App::FeaturePython] Constraint013  label="PlaneCoincident002"  # WARN: FeaturePython — macro-defined, semantics opaque (R4)
  Angle = 0
  AnglePitch = 0
  AngleRoll = 0
  Cascade = false
  Disabled = false
  Group = -> [ElementLink025,ElementLink026]
  LockAngle = false
  Multiply = false
  OffsetX = 0
  OffsetY = 0
  _ConstraintType = 35
  _LinkVersion = 1
  _Parent = -> Constraints
FEATURE [App::FeaturePython] ElementLink025  label="_Element022"  # link proxy (typed FeaturePython)
  LinkTransform = true
  LinkedObject = -> _Element022
  _LinkVersion = 1
  _Parent = -> Constraint013
FEATURE [Part::FeaturePython] _Element022  # link proxy (typed FeaturePython)
  Detach = false
  LinkTransform = true
  LinkedObject = -> Link010 [1.$Element.]
  _LinkVersion = 1
  _Parent = -> Elements
FEATURE [App::FeaturePython] ElementLink026  label="_Element017"  # link proxy (typed FeaturePython)
  LinkTransform = true
  LinkedObject = -> _Element017
  _LinkVersion = 1
  _Parent = -> Constraint013
FEATURE [Part::FeaturePython] _Element023  # link proxy (typed FeaturePython)
  Detach = false
  LinkTransform = true
  LinkedObject = -> Link [Pocket001.Edge6]
  _LinkVersion = 1
  _Parent = -> Elements
FEATURE [App::FeaturePython] Constraint014  label="PlaneCoincident003"  # WARN: FeaturePython — macro-defined, semantics opaque (R4)
  Angle = 0
  AnglePitch = 0
  AngleRoll = 0
  Cascade = false
  Disabled = false
  Group = -> [ElementLink027,ElementLink028]
  LockAngle = false
  Multiply = false
  OffsetX = 0
  OffsetY = 0
  _ConstraintType = 35
  _LinkVersion = 1
  _Parent = -> Constraints
FEATURE [App::FeaturePython] ElementLink027  label="_Element024"  # link proxy (typed FeaturePython)
  LinkTransform = true
  LinkedObject = -> _Element024
  _LinkVersion = 1
  _Parent = -> Constraint014
FEATURE [Part::FeaturePython] _Element024  # link proxy (typed FeaturePython)
  Detach = false
  LinkTransform = true
  LinkedObject = -> Link011 [0.1.$Element002.]
  _LinkVersion = 1
  _Parent = -> Elements
FEATURE [App::FeaturePython] ElementLink028  label="_Element009"  # link proxy (typed FeaturePython)
  LinkTransform = true
  LinkedObject = -> _Element009
  _LinkVersion = 1
  _Parent = -> Constraint014
FEATURE [App::FeaturePython] Constraint015  label="PlaneCoincident004"  # WARN: FeaturePython — macro-defined, semantics opaque (R4)
  Angle = 0
  AnglePitch = 0
  AngleRoll = 0
  Cascade = false
  Disabled = false
  Group = -> [ElementLink029,ElementLink030]
  LockAngle = false
  Multiply = false
  OffsetX = 0
  OffsetY = 0
  _ConstraintType = 35
  _LinkVersion = 1
  _Parent = -> Constraints
FEATURE [App::FeaturePython] ElementLink029  label="_Element025"  # link proxy (typed FeaturePython)
  LinkTransform = true
  LinkedObject = -> _Element025
  _LinkVersion = 1
  _Parent = -> Constraint015
FEATURE [Part::FeaturePython] _Element025  # link proxy (typed FeaturePython)
  Detach = false
  LinkTransform = true
  LinkedObject = -> Link011 [2.1.$Element002.]
  _LinkVersion = 1
  _Parent = -> Elements
FEATURE [App::FeaturePython] ElementLink030  label="_Element003"  # link proxy (typed FeaturePython)
  LinkTransform = true
  LinkedObject = -> _Element003
  _LinkVersion = 1
  _Parent = -> Constraint015
FEATURE [App::FeaturePython] Constraint016  label="PlaneCoincident005"  # WARN: FeaturePython — macro-defined, semantics opaque (R4)
  Angle = 0
  AnglePitch = 0
  AngleRoll = 0
  Cascade = false
  Disabled = false
  Group = -> [ElementLink031,ElementLink032]
  LockAngle = false
  Multiply = false
  OffsetX = 0
  OffsetY = 0
  _ConstraintType = 35
  _LinkVersion = 1
  _Parent = -> Constraints
FEATURE [App::FeaturePython] ElementLink031  label="_Element006"  # link proxy (typed FeaturePython)
  LinkTransform = true
  LinkedObject = -> _Element006
  _LinkVersion = 1
  _Parent = -> Constraint016
FEATURE [App::FeaturePython] ElementLink032  label="_Element026"  # link proxy (typed FeaturePython)
  LinkTransform = true
  LinkedObject = -> _Element026
  _LinkVersion = 1
  _Parent = -> Constraint016
FEATURE [Part::FeaturePython] _Element026  # link proxy (typed FeaturePython)
  Detach = false
  LinkTransform = true
  LinkedObject = -> Link011 [1.1.$Element002.]
  _LinkVersion = 1
  _Parent = -> Elements
FEATURE [App::FeaturePython] Constraint017  label="AxialAlignment003"  # WARN: FeaturePython — macro-defined, semantics opaque (R4)
  Angle = 0
  AnglePitch = 0
  AngleRoll = 0
  Disabled = false
  Group = -> [ElementLink033,ElementLink034]
  LockAngle = false
  Multiply = false
  _ConstraintType = 36
  _LinkVersion = 0
  _Parent = -> Constraints
FEATURE [App::FeaturePython] ElementLink033  label="_Element027"  # link proxy (typed FeaturePython)
  LinkTransform = true
  LinkedObject = -> _Element027
  _LinkVersion = 0
  _Parent = -> Constraint017
FEATURE [Part::FeaturePython] _Element027  # link proxy (typed FeaturePython)
  Detach = false
  LinkTransform = true
  LinkedObject = -> Link007 [2.Pocket003.Face3]
  _LinkVersion = 0
  _Parent = -> Elements
FEATURE [App::FeaturePython] ElementLink034  label="_Element015"  # link proxy (typed FeaturePython)
  LinkTransform = true
  LinkedObject = -> _Element015
  _LinkVersion = 0
  _Parent = -> Constraint017
FEATURE [App::FeaturePython] Constraint018  label="AxialAlignment004"  # WARN: FeaturePython — macro-defined, semantics opaque (R4)
  Angle = 0
  AnglePitch = 0
  AngleRoll = 0
  Disabled = false
  Group = -> [ElementLink035,ElementLink036]
  LockAngle = false
  Multiply = false
  _ConstraintType = 36
  _LinkVersion = 0
  _Parent = -> Constraints
FEATURE [App::FeaturePython] ElementLink035  label="_Element028"  # link proxy (typed FeaturePython)
  LinkTransform = true
  LinkedObject = -> _Element028
  _LinkVersion = 0
  _Parent = -> Constraint018
FEATURE [Part::FeaturePython] _Element028  # link proxy (typed FeaturePython)
  Detach = false
  LinkTransform = true
  LinkedObject = -> Link007 [0.Pocket003.Face3]
  _LinkVersion = 0
  _Parent = -> Elements
FEATURE [App::FeaturePython] ElementLink036  label="_Element015"  # link proxy (typed FeaturePython)
  LinkTransform = true
  LinkedObject = -> _Element015
  _LinkVersion = 0
  _Parent = -> Constraint018
FEATURE [App::FeaturePython] Constraint019  label="PointInPlane"  # WARN: FeaturePython — macro-defined, semantics opaque (R4)
  Disabled = false
  Group = -> [ElementLink037,ElementLink038]
  _ConstraintType = 3
  _LinkVersion = 0
  _Parent = -> Constraints
FEATURE [App::FeaturePython] ElementLink037  label="_Element029"  # link proxy (typed FeaturePython)
  LinkTransform = true
  LinkedObject = -> _Element029
  _LinkVersion = 0
  _Parent = -> Constraint019
FEATURE [Part::FeaturePython] _Element029  # link proxy (typed FeaturePython)
  Detach = false
  LinkTransform = true
  LinkedObject = -> Link007 [0.Pocket003.Vertex323]
  _LinkVersion = 0
  _Parent = -> Elements
FEATURE [App::FeaturePython] ElementLink038  label="_Element017"  # link proxy (typed FeaturePython)
  LinkTransform = true
  LinkedObject = -> _Element017
  _LinkVersion = 0
  _Parent = -> Constraint019
FEATURE [App::FeaturePython] Constraint020  label="PointInPlane001"  # WARN: FeaturePython — macro-defined, semantics opaque (R4)
  Disabled = false
  Group = -> [ElementLink039,ElementLink040]
  _ConstraintType = 3
  _LinkVersion = 0
  _Parent = -> Constraints
FEATURE [App::FeaturePython] ElementLink039  label="_Element030"  # link proxy (typed FeaturePython)
  LinkTransform = true
  LinkedObject = -> _Element030
  _LinkVersion = 0
  _Parent = -> Constraint020
FEATURE [Part::FeaturePython] _Element030  # link proxy (typed FeaturePython)
  Detach = false
  LinkTransform = true
  LinkedObject = -> Link007 [2.Pocket003.Vertex325]
  _LinkVersion = 0
  _Parent = -> Elements
FEATURE [App::FeaturePython] ElementLink040  label="_Element017"  # link proxy (typed FeaturePython)
  LinkTransform = true
  LinkedObject = -> _Element017
  _LinkVersion = 0
  _Parent = -> Constraint020
FEATURE [App::FeaturePython] Constraint021  label="PointsCoincident"  # WARN: FeaturePython — macro-defined, semantics opaque (R4)
  Disabled = false
  Group = -> [ElementLink041,ElementLink042]
  _ConstraintType = 1
  _LinkVersion = 0
  _Parent = -> Constraints
FEATURE [App::FeaturePython] ElementLink041  label="_Element030"  # link proxy (typed FeaturePython)
  LinkTransform = true
  LinkedObject = -> _Element030
  _LinkVersion = 0
  _Parent = -> Constraint021
FEATURE [App::FeaturePython] ElementLink042  label="_Element029"  # link proxy (typed FeaturePython)
  LinkTransform = true
  LinkedObject = -> _Element029
  _LinkVersion = 0
  _Parent = -> Constraint021
FEATURE [App::FeaturePython] Constraint022  label="AxialAlignment005"  # WARN: FeaturePython — macro-defined, semantics opaque (R4)
  Angle = 0
  AnglePitch = 0
  AngleRoll = 0
  Disabled = false
  Group = -> [ElementLink043,ElementLink044]
  LockAngle = false
  Multiply = false
  _ConstraintType = 36
  _LinkVersion = 0
  _Parent = -> Constraints
FEATURE [App::FeaturePython] ElementLink043  label="_Element031"  # link proxy (typed FeaturePython)
  LinkTransform = true
  LinkedObject = -> _Element031
  _LinkVersion = 0
  _Parent = -> Constraint022
FEATURE [Part::FeaturePython] _Element031  # link proxy (typed FeaturePython)
  Detach = false
  LinkTransform = true
  LinkedObject = -> Link007 [1.Pocket003.Face3]
  _LinkVersion = 0
  _Parent = -> Elements
FEATURE [App::FeaturePython] ElementLink044  label="_Element015"  # link proxy (typed FeaturePython)
  LinkTransform = true
  LinkedObject = -> _Element015
  _LinkVersion = 0
  _Parent = -> Constraint022
FEATURE [App::FeaturePython] Constraint023  label="PointInPlane002"  # WARN: FeaturePython — macro-defined, semantics opaque (R4)
  Disabled = false
  Group = -> [ElementLink045,ElementLink046]
  _ConstraintType = 3
  _LinkVersion = 0
  _Parent = -> Constraints
FEATURE [App::FeaturePython] ElementLink045  label="_Element032"  # link proxy (typed FeaturePython)
  LinkTransform = true
  LinkedObject = -> _Element032
  _LinkVersion = 0
  _Parent = -> Constraint023
FEATURE [Part::FeaturePython] _Element032  # link proxy (typed FeaturePython)
  Detach = false
  LinkTransform = true
  LinkedObject = -> Link007 [1.Pocket003.Vertex323]
  _LinkVersion = 0
  _Parent = -> Elements
FEATURE [App::FeaturePython] ElementLink046  label="_Element017"  # link proxy (typed FeaturePython)
  LinkTransform = true
  LinkedObject = -> _Element017
  _LinkVersion = 0
  _Parent = -> Constraint023
FEATURE [App::FeaturePython] Constraint024  label="PointsCoincident001"  # WARN: FeaturePython — macro-defined, semantics opaque (R4)
  Disabled = false
  Group = -> [ElementLink047,ElementLink048]
  _ConstraintType = 1
  _LinkVersion = 0
  _Parent = -> Constraints
FEATURE [App::FeaturePython] ElementLink047  label="_Element032"  # link proxy (typed FeaturePython)
  LinkTransform = true
  LinkedObject = -> _Element032
  _LinkVersion = 0
  _Parent = -> Constraint024
FEATURE [App::FeaturePython] ElementLink048  label="_Element033"  # link proxy (typed FeaturePython)
  LinkTransform = true
  LinkedObject = -> _Element033
  _LinkVersion = 0
  _Parent = -> Constraint024
FEATURE [Part::FeaturePython] _Element033  # link proxy (typed FeaturePython)
  Detach = false
  LinkTransform = true
  LinkedObject = -> Link007 [0.Pocket003.Vertex325]
  _LinkVersion = 0
  _Parent = -> Elements
